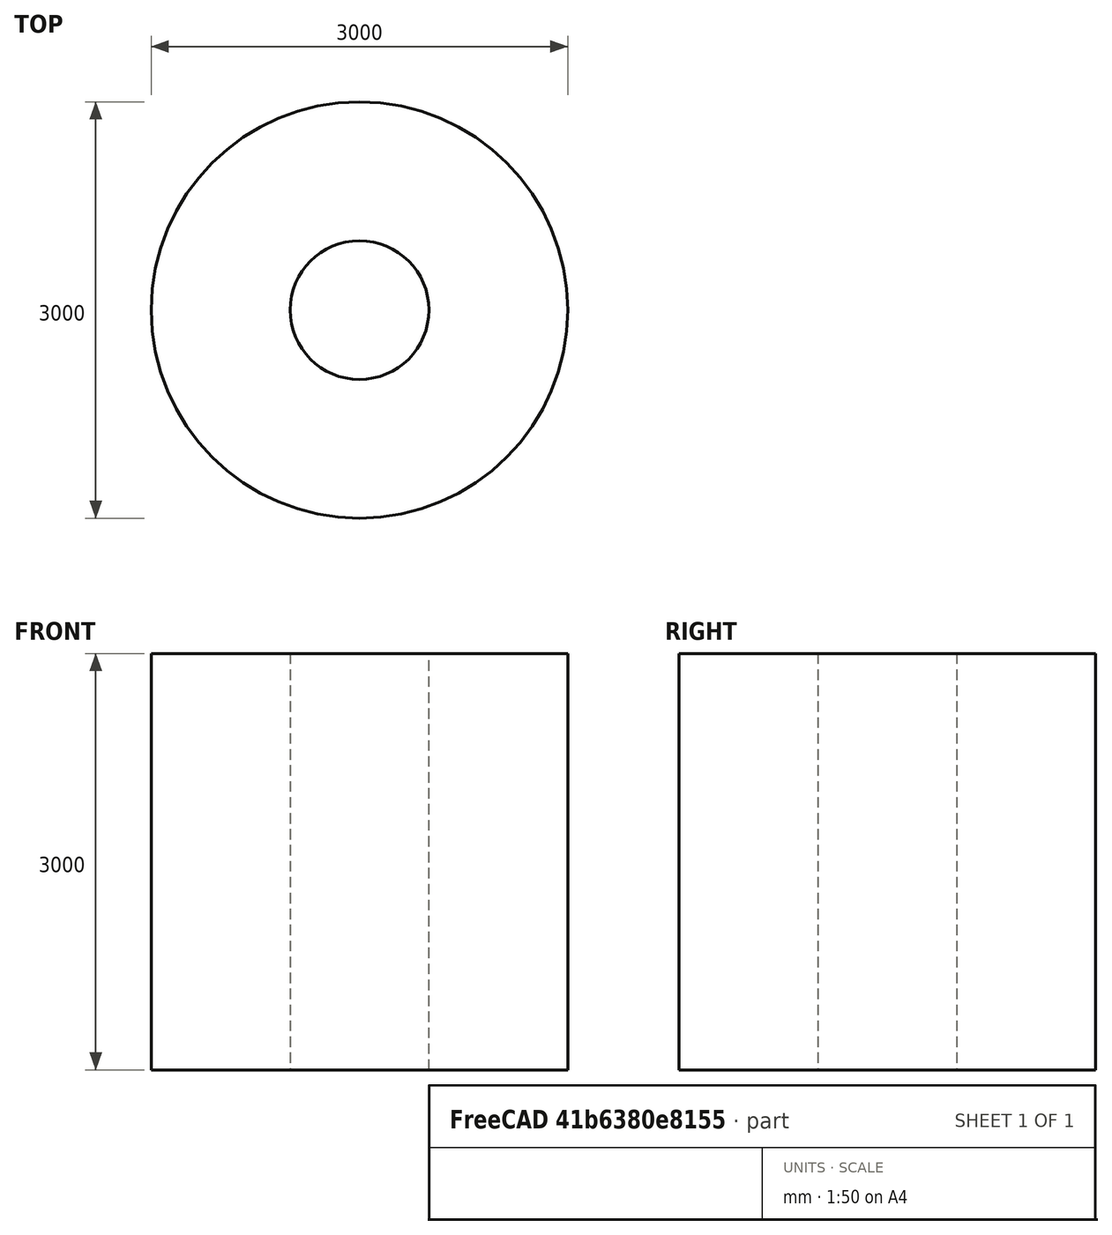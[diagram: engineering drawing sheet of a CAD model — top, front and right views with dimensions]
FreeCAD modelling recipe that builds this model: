
FCSTD DOCUMENT  (FreeCAD 1.0R39109 (Git))
Label: walec z izolacją
License: All rights reserved
LicenseURL: http://en.wikipedia.org/wiki/All_rights_reserved
objects: Sketcher::SketchObject×1, PartDesign::Pad×1, PartDesign::Body×1, Fem::FemSolverObjectPython×1, App::MaterialObjectPython×1, Fem::ConstraintInitialTemperature×1, Fem::FemMeshShapeBaseObjectPython×1, Fem::ConstraintHeatflux×1, Fem::FemAnalysis×1
note: 6 computed .brp shape members not serialized (recipe doc carries the construction recipe); baked Part::Feature solids carry a one-line shape summary decoded from their .brp

FEATURE [Sketcher::SketchObject] Sketch
  ArcFitTolerance = 1e-06
  AttachmentSupport = -> [XY_Plane]
  FullyConstrained = true
  MakeInternals = false
  MapMode = 2
  sketch-geometry (2):
    g0: Circle CenterX=0 CenterY=0 CenterZ=0 NormalX=0 NormalY=0 NormalZ=1 AngleXU=0 Radius=500
    g1: Circle CenterX=0 CenterY=0 CenterZ=0 NormalX=0 NormalY=0 NormalZ=1 AngleXU=0 Radius=1500
  constraints (4):
    c: Coincident(g0,g-1)
    c: Coincident(g1,g0)
    c: Diameter(g0) = 1000
    c: Distance(g0,g1) = 1000
FEATURE [PartDesign::Pad] Pad
  Direction = (0,0,1)
  Length = 3000
  Length2 = 10
  Profile = -> Sketch
  ReferenceAxis = -> Sketch [N_Axis]
  Refine = true
  Suppressed = false
  Type = 0
FEATURE [PartDesign::Body] Body  label="Zawartość"
  AllowCompound = false
  Group = -> [Sketch,Pad]
  Origin = -> Origin
  Tip = -> Pad
FEATURE [Fem::FemSolverObjectPython] SolverCcxTools  # FEM object (typed FeaturePython)
  AnalysisType = 2
  BeamReducedIntegration = true
  BeamShellResultOutput3D = true
  BucklingFactors = 1
  EigenmodeHighLimit = 1000000
  EigenmodeLowLimit = 0
  EigenmodesCount = 10
  GeometricalNonlinearity = 0
  IterationsControlParameterCutb = 0.25,0.5,0.75,0.85,,,1.5,
  IterationsControlParameterIter = 4,8,9,200,10,400,,200,,
  IterationsControlParameterTimeUse = false
  IterationsMaximum = 2000
  IterationsUserDefinedIncrementations = false
  IterationsUserDefinedTimeStepLength = false
  MaterialNonlinearity = 0
  MatrixSolverType = 0
  ModelSpace = 0
  OutputFrequency = 1
  SplitInputWriter = false
  ThermoMechSteadyState = true
  ThermoMechType = 0
  TimeEnd = 1
  TimeInitialStep = 1
  TimeMaximumStep = 1
  TimeMinimumStep = 1e-05
FEATURE [App::MaterialObjectPython] MaterialSolid  # material (typed FeaturePython)
  Category = 0
  Material = Author=Juergen Riegel,AuthorAndLicense=CC-BY-3.0,CardName=ABS-Generic,Density=1.06e-06 kg/mm^3,+12 more (map truncated)
  References = -> [Pad]
  UUID = 73371529-2983-47dd-b988-6739a2e20029
FEATURE [Fem::ConstraintInitialTemperature] ConstraintInitialTemperature
  NormalDirection = (0,0,1)
  Suppressed = false
  initialTemperature = 300
FEATURE [Fem::FemMeshShapeBaseObjectPython] FEMMeshGmsh  # FEM object (typed FeaturePython)
  Algorithm2D = 0
  Algorithm3D = 0
  CharacteristicLengthMax = 0
  CharacteristicLengthMin = 0
  CoherenceMesh = true
  ElementDimension = 0
  ElementOrder = 1
  GeometryTolerance = 1e-06
  GroupsOfNodes = false
  HighOrderOptimize = 0
  MeshSizeFromCurvature = 12
  OptimizeNetgen = false
  OptimizeStd = true
  RecombinationAlgorithm = 0
  Recombine3DAll = false
  RecombineAll = false
  SecondOrderLinear = false
  Shape = -> Pad
  SubdivisionAlgorithm = 0
FEATURE [Fem::ConstraintHeatflux] ConstraintHeatflux
  AmbientTemp = 1300
  ConstraintType = 1
  DFlux = 0
  Emissivity = 1
  FilmCoef = 10
  NormalDirection = (1,-1e-16,0)
  Normals = (16) [(-1,0,0),(0.5,-0.866025,0),(0.5,0.866025,0),(-1,2.44929e-16,0),(-1,0,0),(0.5,-0.866025,0),(0.5,0.866025,0),(-1,2.44929e-16,0),(-1,0,0),+7 more]
  Points = (16) [(500,0,3000),(-250,433.013,3000),(-250,-433.013,3000),(500,-1.22465e-13,3000),(500,0,2000),(-250,433.013,2000),(-250,-433.013,2000),+9 more]
  References = -> [Pad]
  Suppressed = false
FEATURE [Fem::FemAnalysis] Analysis
  Group = -> [SolverCcxTools,MaterialSolid,ConstraintInitialTemperature,FEMMeshGmsh,ConstraintHeatflux]
